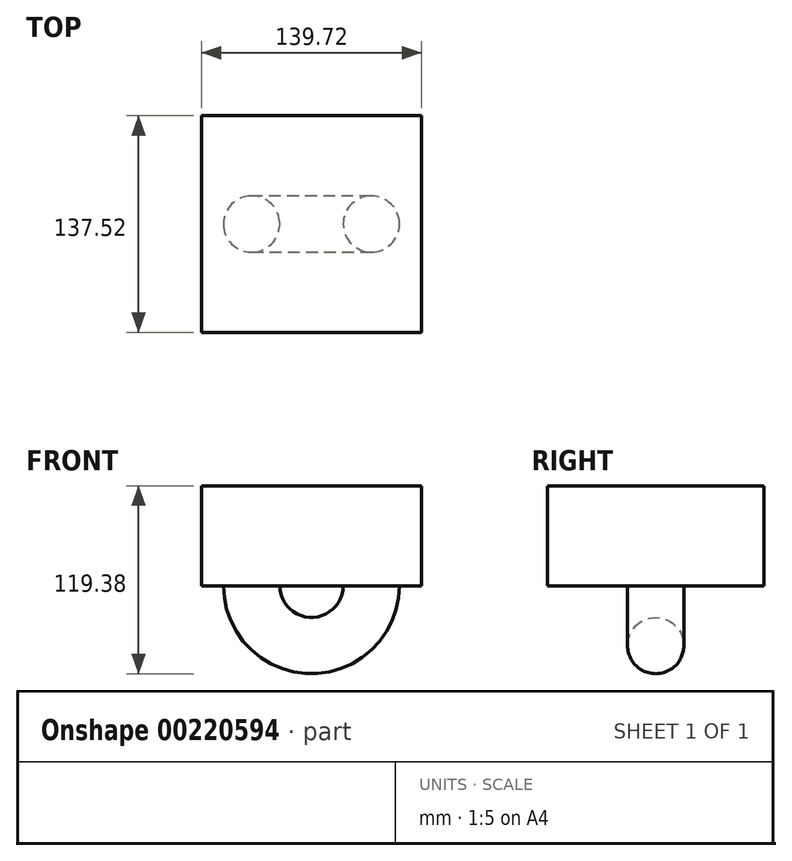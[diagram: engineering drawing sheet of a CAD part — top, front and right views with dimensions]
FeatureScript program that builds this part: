
annotation { "Feature Type Name" : "Feature", "Feature Type Description" : "" }
export const myFeature = defineFeature(function(context is Context, id is Id, definition is map)
    precondition{}
    {
        {
            var Q0;
            Q0=qCreatedBy(makeId("Top.planeOp"),FACE);
            var sketch = newSketch(context, id + "F0", { "sketchPlane" : qUnion([Q0])});
            skLineSegment(sketch, "E0.bottom", {"start": v(69.86, -68.76) * mm, "end": v(-69.86, -68.76) * mm});
            skLineSegment(sketch, "E0.top", {"start": v(69.86, 68.76) * mm, "end": v(-69.86, 68.76) * mm});
            skLineSegment(sketch, "E0.left", {"start": v(69.86, -68.76) * mm, "end": v(69.86, 68.76) * mm});
            skLineSegment(sketch, "E0.right", {"start": v(-69.86, -68.76) * mm, "end": v(-69.86, 68.76) * mm});
            skPoint(sketch, "E0.middle", {"position": v(0, 0) * mm});
            skLineSegment(sketch, "E1", {"start": v(0, 68.76) * mm, "end": v(0, -68.76) * mm});
            skSolve(sketch);
        }
        {
            var Q0;
            {var subQ0=sQuery(id+"F0.wireOp",EDGE,"E0.left");Q0=makeQuery(id+"F0.imprint","IMPRINT",FACE,{"disambiguationData":[TD([[makeQuery(id+"F0.imprint","IMPRINT",EDGE,{"derivedFrom":subQ0}),1.0]])]});}
            var Q1;
            {var subQ0=sQuery(id+"F0.wireOp",EDGE,"E0.right");Q1=makeQuery(id+"F0.imprint","IMPRINT",FACE,{"disambiguationData":[TD([[makeQuery(id+"F0.imprint","IMPRINT",EDGE,{"derivedFrom":subQ0}),-1.0]])]});}
            extrude(context, id + "F1", {"entities" : qUnion([Q0, Q1]), "depth" : 63.5 * mm});
        }
        {
            var Q0;
            {var subQ0=sQuery(id+"F0.wireOp",EDGE,"E0.left");Q0=makeQuery(id+"F0.imprint","IMPRINT",FACE,{"disambiguationData":[TD([[makeQuery(id+"F0.imprint","IMPRINT",EDGE,{"derivedFrom":subQ0}),1.0]])]});}
            var sketch = newSketch(context, id + "F2", { "sketchPlane" : qUnion([Q0])});
            skCircle(sketch, "E2", {"center": v(38, 0) * mm, "radius": 17.87 * mm});
            skSolve(sketch);
        }
        {
            var Q0;
            Q0=makeQuery(id+"F2.imprint","IMPRINT",FACE,{"disambiguationData":[TD([[makeQuery(id+"F2.imprint","IMPRINT",EDGE,{"derivedFrom":sQuery(id+"F2.wireOp",EDGE,"E2")}),1.0]])]});
            var Q1;
            Q1=sQuery(id+"F0.wireOp",EDGE,"E1");
            revolve(context, id + "F3", {"operationType" : NewBodyOperationType.ADD, "entities" : qUnion([Q0]), "axis" : qUnion([Q1]), "revolveType" : RevolveType.FULL});
        }
    });
